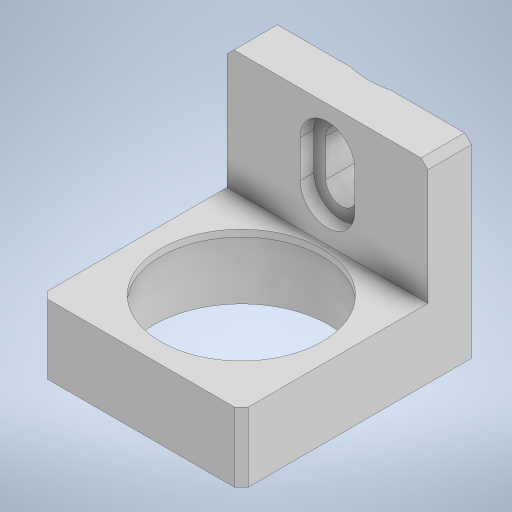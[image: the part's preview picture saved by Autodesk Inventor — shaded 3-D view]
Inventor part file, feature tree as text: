
AUTODESK INVENTOR PART (.ipt)
format: ipt  version: 2024.2 (Build 282272000, 272)  size: 402,944 bytes
history: native  units: in
note: dims shown in document units (in); Inventor stores cm internally (conversion verified against a paired STEP export)
features: extrude x8, other x2, sketch x2, hole x1, chamfer x1
ambient origin geometry x8: Origin, YZ Plane, XZ Plane, XY Plane, X Axis, Y Axis, Z Axis, Center Point
bodies: Body1 (feature_tree)
feature tree (14):
  other  "ADAPTER_SM1"
  other  "Table"
  extrude  "Extrusion3"  Depth=0.5807in
  extrude  "Extrusion4"  Depth=0.3937in TaperAngle=0.0deg
  sketch  "Sketch9"  dims[d24=1.1102in d26=0.5807in]
  extrude  "Extrusion6"  TaperAngle=0.0deg  [1 undecoded]
  hole  "Hole3"  [1 undecoded]
  extrude  "Extrusion7"  TaperAngle=0.0deg  [1 undecoded]
  extrude  "Extrusion8"  TaperAngle=0.0deg  [1 undecoded]
  extrude  "Extrusion9"  Depth=0.3937in TaperAngle=0.0deg
  extrude  "Extrusion10"  Depth=0.3937in TaperAngle=0.0deg
  chamfer  "Chamfer10"  Distance=0.3622in
  extrude  "Extrusion11"  TaperAngle=0.0deg  [1 undecoded]
  sketch  "Sketch11"  dims[d28=0.4016in d29=0.252in d30=0.0in d31=0.0in d32=0.0in d33=0.0in d34=0.0in d35=1.0787in d36=0.0in d77=0.0827in d78=0.0in d85=0.0827in d86=0.328in d87=0.297in d88=0.11in d89=90.0deg d90=0.0827in d91=0.0in d93=0.3622in d94=0.0in d96=0.0in d97=0.0in d98=0.9331in d99=0.3622in d100=0.0in d131=0.3543in d134=0.1727in d135=0.0in d136=0.315in d137=0.315in d138=0.0in d139=0.2165in d140=0.0in d141=0.1083in d142=0.3543in d143=0.1728in d144=0.0in d183=0.7087in d185=0.0886in d186=0.2165in d187=0.0in d188=0.3543in d189=0.0413in d190=0.0392in d191=0.0in d192=0.1969in d193=0.0394in d194=0.0787in d195=45.0deg d196=0.0in d197=1.0in d198=0.7382in d199=0.3937in d200=0.0in d201=0.75in d202=0.5807in]
note: 5 required parameter values undecoded (feature->parameter linkage not recoverable at this tier; creation-order binding heuristic only, values carry confidence <= 0.55)
